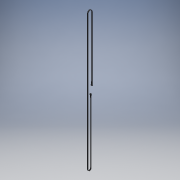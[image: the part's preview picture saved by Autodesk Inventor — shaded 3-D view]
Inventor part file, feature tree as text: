
AUTODESK INVENTOR PART (.ipt)
format: ipt  version: 2017 SP1 (Build 210196100, 196)  size: 156,672 bytes
history: native  units: in
note: dims shown in document units (in); Inventor stores cm internally (conversion verified against a paired STEP export)
features: extrude x1, sketch x1
ambient origin geometry x8: Origin, YZ Plane, XZ Plane, XY Plane, X Axis, Y Axis, Z Axis, Center Point
bodies: Solid1 (feature_tree)
feature tree (2):
  extrude  "Extrusion1"  Depth=0.5in
  sketch  "Sketch1"  dims[d1=0.5625in d2=0.5in d4=0.25in d5=0.0625in d6=2.375in d7=0.25in d8=0.5in d9=0.5in d10=0.005in d11=0.25in d12=0.5in d13=0.005in d14=0.5in d15=47.0in d16=0.375in d17=0.0in]
